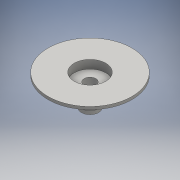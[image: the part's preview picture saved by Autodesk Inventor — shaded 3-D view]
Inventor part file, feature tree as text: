
AUTODESK INVENTOR PART (.ipt)
format: ipt  version: 2016 SP1 (Build 200210100, 210)  size: 144,384 bytes
history: native  units: mm
features: sketch x4, extrude x3, revolve x1
ambient origin geometry x8: Origin, YZ Plane, XZ Plane, XY Plane, X Axis, Y Axis, Z Axis, Center Point
bodies: Solid1 (feature_tree)
feature tree (8):
  extrude  "Extrusion1"  Depth=60.0mm
  revolve  "Revolution1"  Angle=90.0deg
  extrude  "Extrusion2"  Depth=6.0mm TaperAngle=0.0deg
  extrude  "Extrusion3"  Depth=4.0mm
  sketch  "Sketch1"  dims[d0=22.6mm d1=60.0mm]
  sketch  "Sketch2"  dims[d2=6.0mm d3=0.0mm d4=90.0deg]
  sketch  "Sketch3"  dims[d5=8.4mm d6=6.0mm d7=0.0mm]
  sketch  "Sketch4"  dims[d8=4.0mm d9=60.0mm d11=4.0mm d12=10.0mm d14=10.0mm d16=48.0mm d17=4.0mm d18=0.0mm]
